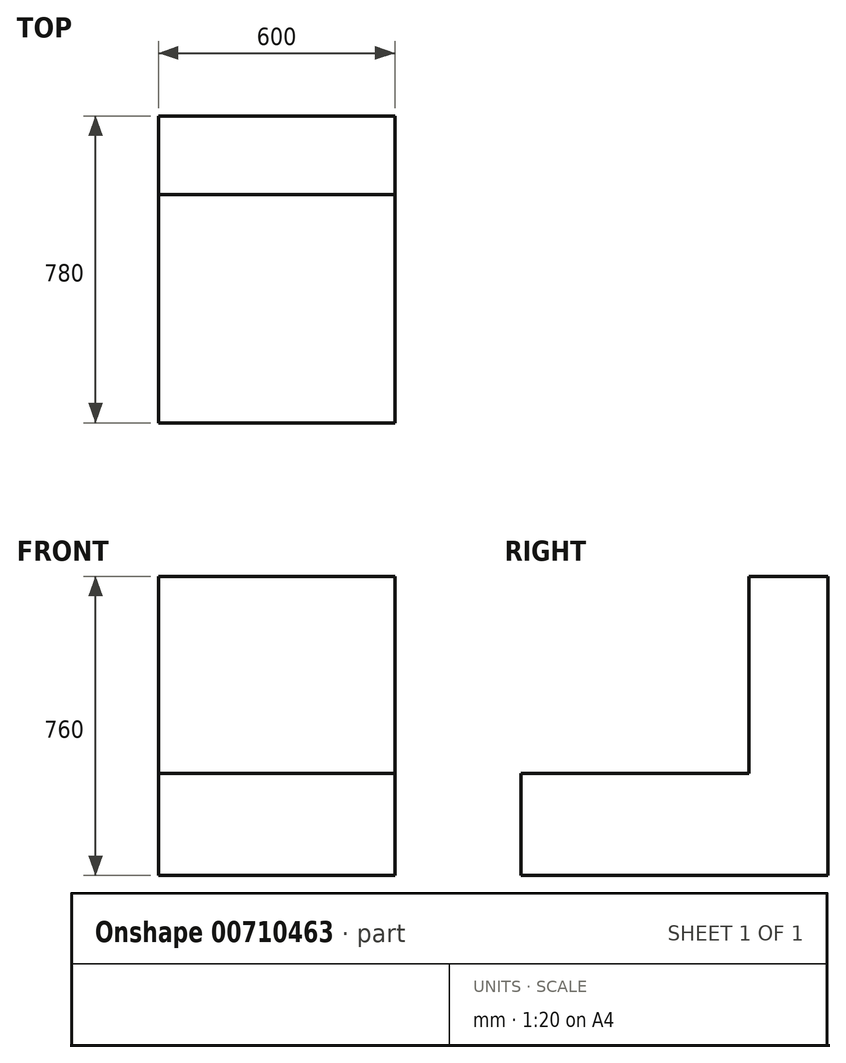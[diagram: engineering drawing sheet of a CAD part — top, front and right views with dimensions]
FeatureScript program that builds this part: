
annotation { "Feature Type Name" : "Feature", "Feature Type Description" : "" }
export const myFeature = defineFeature(function(context is Context, id is Id, definition is map)
    precondition{}
    {
        {
            var Q0;
            Q0=qCreatedBy(makeId("Top.planeOp"),FACE);
            var sketch = newSketch(context, id + "F0", { "sketchPlane" : qUnion([Q0])});
            skLineSegment(sketch, "E0.bottom", {"start": v(300, 390) * mm, "end": v(-300, 390) * mm});
            skLineSegment(sketch, "E0.top", {"start": v(300, -390) * mm, "end": v(-300, -390) * mm});
            skLineSegment(sketch, "E0.left", {"start": v(300, 390) * mm, "end": v(300, -390) * mm});
            skLineSegment(sketch, "E0.right", {"start": v(-300, 390) * mm, "end": v(-300, -390) * mm});
            skPoint(sketch, "E0.middle", {"position": v(0, 0) * mm});
            skSolve(sketch);
        }
        {
            var Q0;
            Q0=makeQuery(id+"F0.imprint","IMPRINT",FACE,{"disambiguationData":[TD([[makeQuery(id+"F0.imprint","IMPRINT",EDGE,{"derivedFrom":sQuery(id+"F0.wireOp",EDGE,"E0.bottom")}),1.0]])]});
            extrude(context, id + "F1", {"entities" : qUnion([Q0]), "depth" : 760 * mm, "offsetDistance" : 25 * mm});
        }
        {
            var Q0;
            Q0=makeQuery(id+"F1.opExtrude","CAP_FACE",FACE,{"disambiguationData":[OSD([sQuery(id+"F0.wireOp",EDGE,"E0.bottom"),sQuery(id+"F0.wireOp",EDGE,"E0.top"),sQuery(id+"F0.wireOp",EDGE,"E0.left"),sQuery(id+"F0.wireOp",EDGE,"E0.right")])],"isStart":false});
            var sketch = newSketch(context, id + "F2", { "sketchPlane" : qUnion([Q0])});
            skLineSegment(sketch, "E1.bottom", {"start": v(-300, -390) * mm, "end": v(300, -390) * mm});
            skLineSegment(sketch, "E1.top", {"start": v(-300, 190) * mm, "end": v(300, 190) * mm});
            skLineSegment(sketch, "E1.left", {"start": v(-300, -390) * mm, "end": v(-300, 190) * mm});
            skLineSegment(sketch, "E1.right", {"start": v(300, -390) * mm, "end": v(300, 190) * mm});
            skSolve(sketch);
        }
        {
            var Q0;
            Q0 = qSketchRegion(id + "F2", true);
            extrude(context, id + "F3", {"entities" : qUnion([Q0]), "operationType" : NewBodyOperationType.REMOVE, "oppositeDirection" : true, "depth" : 500 * mm, "offsetDistance" : 25 * mm});
        }
    });
